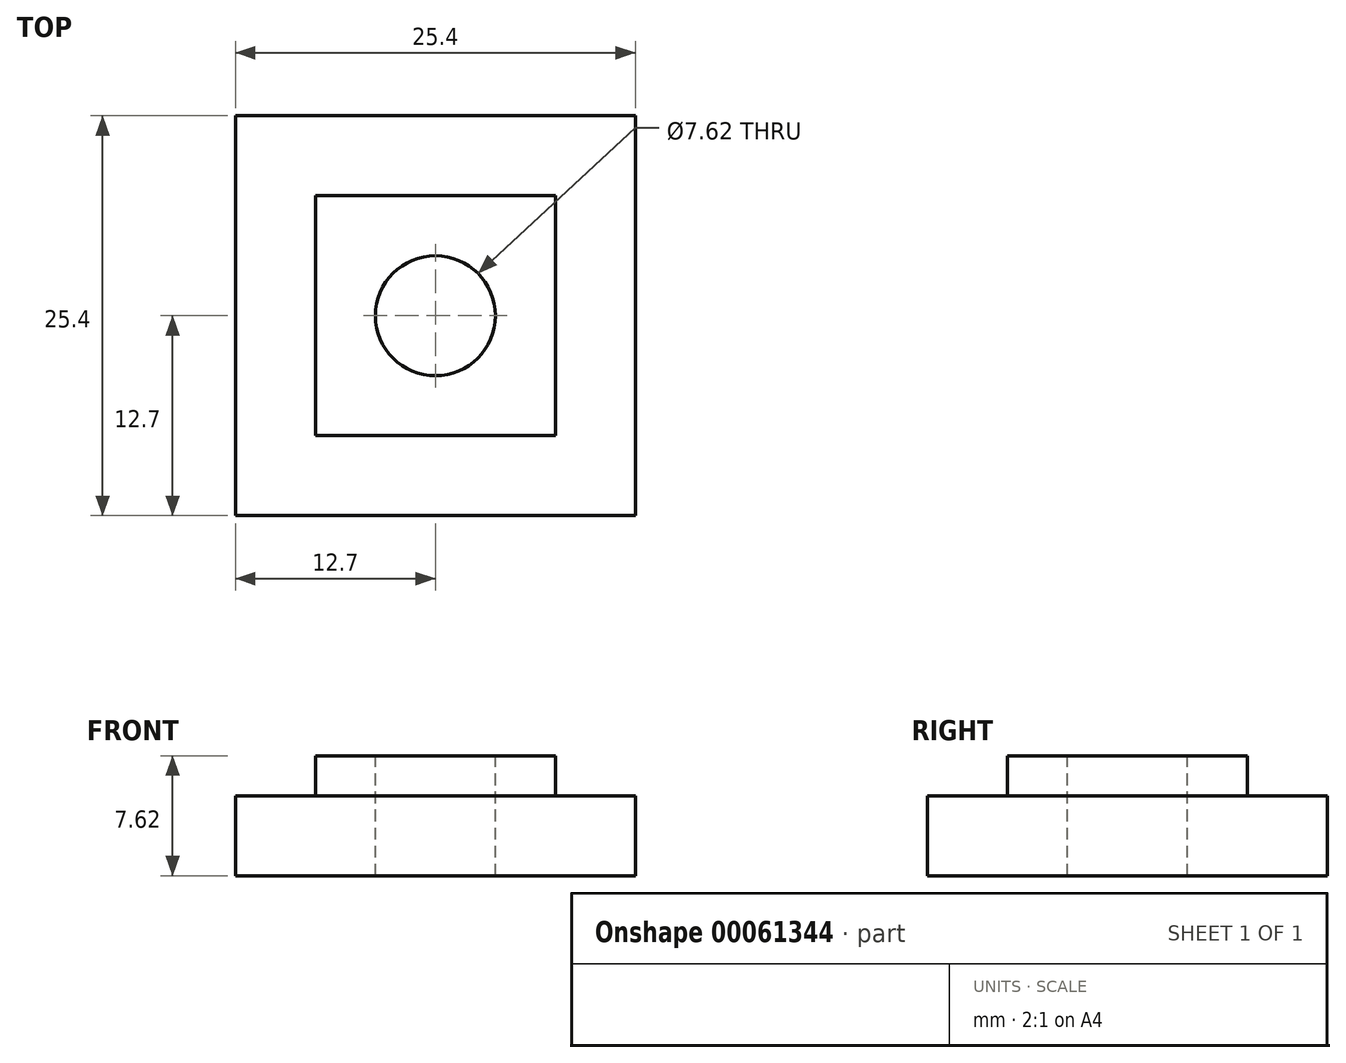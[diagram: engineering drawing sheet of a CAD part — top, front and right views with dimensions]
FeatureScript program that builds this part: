
annotation { "Feature Type Name" : "Feature", "Feature Type Description" : "" }
export const myFeature = defineFeature(function(context is Context, id is Id, definition is map)
    precondition{}
    {
        {
            var Q0;
            Q0=qCreatedBy(makeId("Top.planeOp"),FACE);
            var sketch = newSketch(context, id + "F0", { "sketchPlane" : qUnion([Q0])});
            skLineSegment(sketch, "E0.bottom", {"start": v(0, 0) * mm, "end": v(25.4, 0) * mm});
            skLineSegment(sketch, "E0.top", {"start": v(0, 25.4) * mm, "end": v(25.4, 25.4) * mm});
            skLineSegment(sketch, "E0.left", {"start": v(0, 0) * mm, "end": v(0, 25.4) * mm});
            skLineSegment(sketch, "E0.right", {"start": v(25.4, 0) * mm, "end": v(25.4, 25.4) * mm});
            skSolve(sketch);
        }
        {
            var Q0;
            Q0 = qSketchRegion(id + "F0", true);
            extrude(context, id + "F1", {"entities" : qUnion([Q0]), "depth" : 5.08 * mm});
        }
        {
            var Q0;
            Q0=makeQuery(id+"F1.opExtrude","CAP_FACE",FACE,{"disambiguationData":[OSD([sQuery(id+"F0.wireOp",EDGE,"E0.bottom"),sQuery(id+"F0.wireOp",EDGE,"E0.top"),sQuery(id+"F0.wireOp",EDGE,"E0.left"),sQuery(id+"F0.wireOp",EDGE,"E0.right")])],"isStart":false});
            var sketch = newSketch(context, id + "F2", { "sketchPlane" : qUnion([Q0])});
            skLineSegment(sketch, "E1.bottom", {"start": v(5.08, 20.32) * mm, "end": v(20.32, 20.32) * mm});
            skLineSegment(sketch, "E1.top", {"start": v(5.08, 5.08) * mm, "end": v(20.32, 5.08) * mm});
            skLineSegment(sketch, "E1.left", {"start": v(5.08, 20.32) * mm, "end": v(5.08, 5.08) * mm});
            skLineSegment(sketch, "E1.right", {"start": v(20.32, 20.32) * mm, "end": v(20.32, 5.08) * mm});
            skSolve(sketch);
        }
        {
            var Q0;
            Q0 = qSketchRegion(id + "F2", true);
            extrude(context, id + "F3", {"entities" : qUnion([Q0]), "operationType" : NewBodyOperationType.ADD, "depth" : 2.54 * mm});
        }
        {
            var Q0;
            Q0=makeQuery(id+"F3.opExtrude","CAP_FACE",FACE,{"disambiguationData":[OSD([sQuery(id+"F2.wireOp",EDGE,"E1.bottom"),sQuery(id+"F2.wireOp",EDGE,"E1.top"),sQuery(id+"F2.wireOp",EDGE,"E1.left"),sQuery(id+"F2.wireOp",EDGE,"E1.right")])],"isStart":false});
            var sketch = newSketch(context, id + "F4", { "sketchPlane" : qUnion([Q0])});
            skCircle(sketch, "E2", {"center": v(12.7, 12.7) * mm, "radius": 3.81 * mm});
            skPoint(sketch, "E2.centerSnap0", {"position": v(12.7, 5.08) * mm});
            skPoint(sketch, "E2.centerSnap1", {"position": v(5.08, 12.7) * mm});
            skSolve(sketch);
        }
        {
            var Q0;
            Q0 = qSketchRegion(id + "F4", true);
            extrude(context, id + "F5", {"entities" : qUnion([Q0]), "operationType" : NewBodyOperationType.REMOVE, "oppositeDirection" : true, "depth" : 25.4 * mm});
        }
    });
